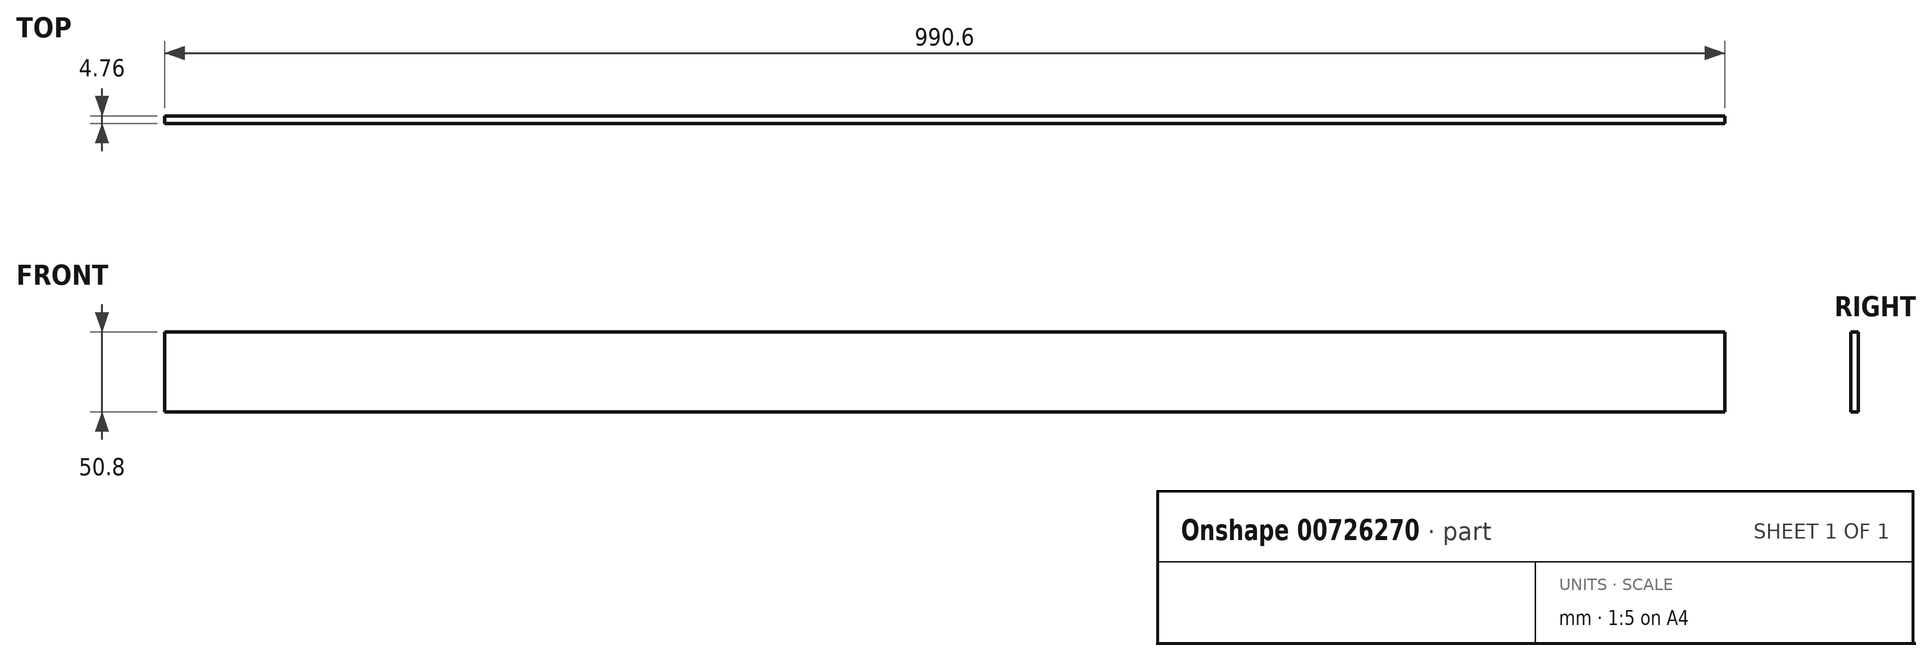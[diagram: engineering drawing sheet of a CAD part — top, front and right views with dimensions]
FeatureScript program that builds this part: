
annotation { "Feature Type Name" : "Feature", "Feature Type Description" : "" }
export const myFeature = defineFeature(function(context is Context, id is Id, definition is map)
    precondition{}
    {
        {
            var Q0;
            Q0=qCreatedBy(makeId("Front.planeOp"),FACE);
            var sketch = newSketch(context, id + "F0", { "sketchPlane" : qUnion([Q0])});
            skLineSegment(sketch, "E0.bottom", {"start": v(495.3, 25.4) * mm, "end": v(-495.3, 25.4) * mm});
            skLineSegment(sketch, "E0.top", {"start": v(495.3, -25.4) * mm, "end": v(-495.3, -25.4) * mm});
            skLineSegment(sketch, "E0.left", {"start": v(495.3, 25.4) * mm, "end": v(495.3, -25.4) * mm});
            skLineSegment(sketch, "E0.right", {"start": v(-495.3, 25.4) * mm, "end": v(-495.3, -25.4) * mm});
            skPoint(sketch, "E0.middle", {"position": v(0, 0) * mm});
            skSolve(sketch);
        }
        {
            var Q0;
            Q0 = qSketchRegion(id + "F0", true);
            extrude(context, id + "F1", {"entities" : qUnion([Q0]), "depth" : 4.76 * mm, "offsetDistance" : 25.4 * mm});
        }
    });
